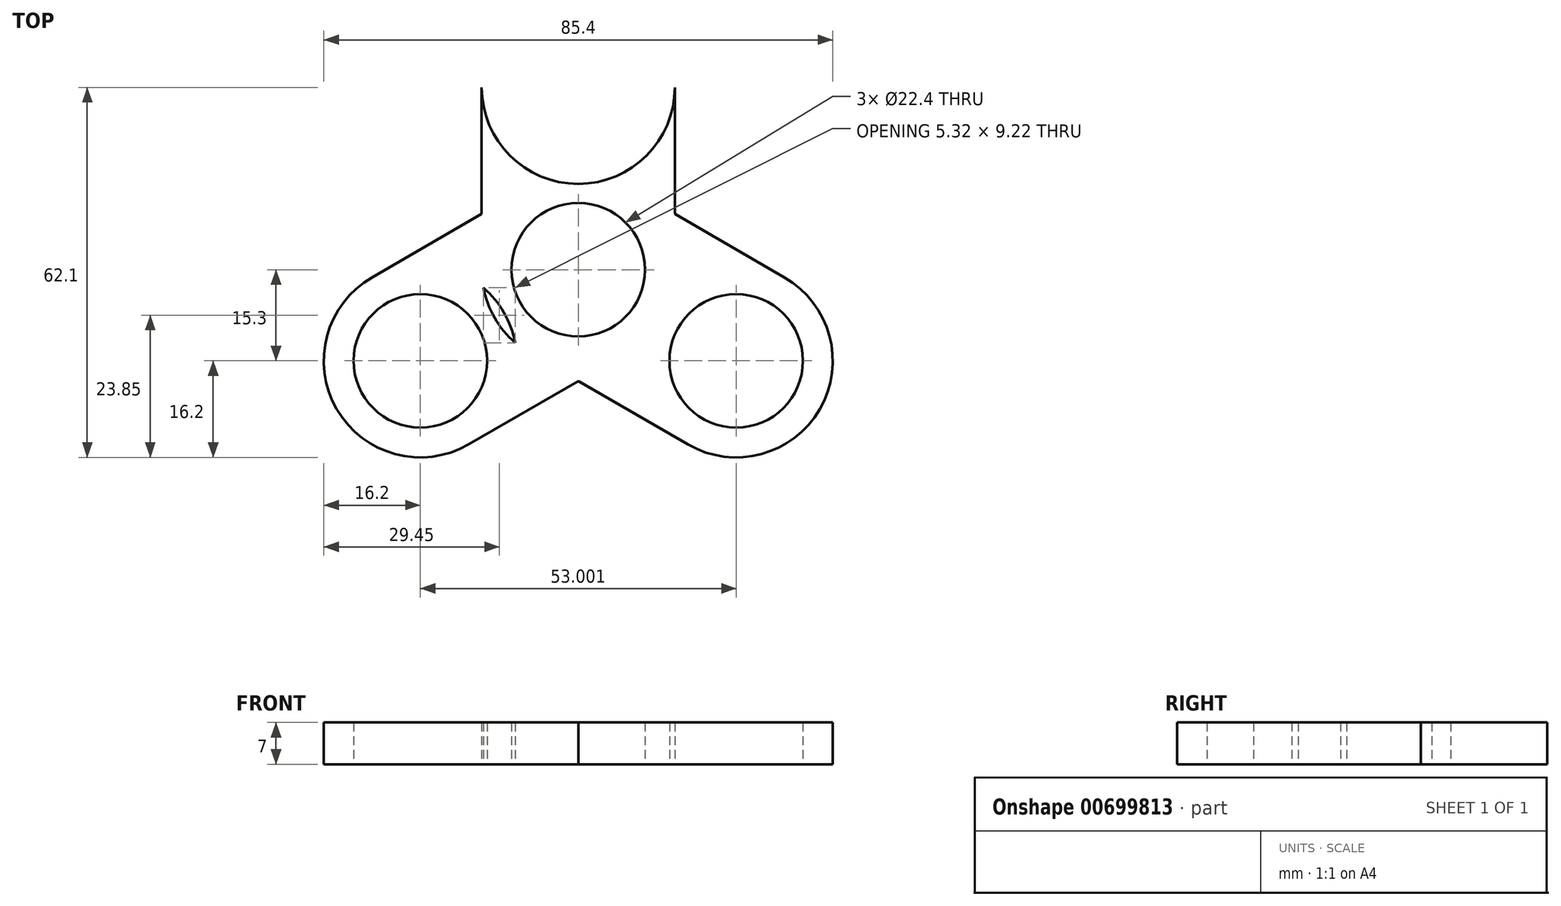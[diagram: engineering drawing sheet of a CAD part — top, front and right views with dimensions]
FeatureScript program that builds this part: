
annotation { "Feature Type Name" : "Feature", "Feature Type Description" : "" }
export const myFeature = defineFeature(function(context is Context, id is Id, definition is map)
    precondition{}
    {
        {
            var Q0;
            Q0=qCreatedBy(makeId("Top.planeOp"),FACE);
            var sketch = newSketch(context, id + "F0", { "sketchPlane" : qUnion([Q0])});
            skCircle(sketch, "E0", {"center": v(0, 0) * mm, "radius": 11.2 * mm});
            skCircle(sketch, "E1", {"center": v(0, 0) * mm, "radius": 50 * mm});
            skLineSegment(sketch, "E2", {"start": v(0, 50) * mm, "end": v(0, 11.2) * mm});
            skCircle(sketch, "E3", {"center": v(0, 30.6) * mm, "radius": 11.2 * mm});
            skCircle(sketch, "E4", {"center": v(0, 0) * mm, "radius": 16.2 * mm});
            skCircle(sketch, "E5", {"center": v(0, 30.6) * mm, "radius": 16.2 * mm});
            skLineSegment(sketch, "E6", {"start": v(16.2, 30.6) * mm, "end": v(16.2, 0) * mm});
            skLineSegment(sketch, "E7", {"start": v(0, 60) * mm, "end": v(0, -58.02) * mm, "construction": true});
            skLineSegment(sketch, "E8.MirrorCS", {"start": v(-16.2, 30.6) * mm, "end": v(-16.2, 0) * mm});
            skLineSegment(sketch, "E9.1.0", {"start": v(-18.4, -29.33) * mm, "end": v(8.1, -14.03) * mm});
            skCircle(sketch, "E9.1.2", {"center": v(-26.5, -15.3) * mm, "radius": 16.2 * mm});
            skCircle(sketch, "E9.1.3", {"center": v(-26.5, -15.3) * mm, "radius": 11.2 * mm});
            skLineSegment(sketch, "E9.1.4", {"start": v(-34.6, -1.27) * mm, "end": v(-8.1, 14.03) * mm});
            skLineSegment(sketch, "E9.2.0", {"start": v(34.6, -1.27) * mm, "end": v(8.1, 14.03) * mm});
            skCircle(sketch, "E9.2.2", {"center": v(26.5, -15.3) * mm, "radius": 16.2 * mm});
            skCircle(sketch, "E9.2.3", {"center": v(26.5, -15.3) * mm, "radius": 11.2 * mm});
            skLineSegment(sketch, "E9.2.4", {"start": v(18.4, -29.33) * mm, "end": v(-8.1, -14.03) * mm});
            skSolve(sketch);
        }
        {
            var Q0;
            Q0=makeQuery(id+"F0.imprint","IMPRINT",FACE,{"disambiguationData":[TD([[makeQuery(id+"F0.imprint","IMPRINT",EDGE,{"derivedFrom":sQuery(id+"F0.wireOp",EDGE,"E9.1.3")}),-1.0]])]});
            var Q1;
            {var subQ0=sQuery(id+"F0.wireOp",EDGE,"E4");var subQ1=sQuery(id+"F0.wireOp",EDGE,"E8.MirrorCS");var subQ2=makeQuery(id+"F0.imprint","INTERSECT",VERTEX,{"derivedFrom":[subQ1,subQ0]});Q1=makeQuery(id+"F0.imprint","IMPRINT",FACE,{"disambiguationData":[TD([[makeQuery(id+"F0.imprint","IMPRINT",EDGE,{"disambiguationData":[TD([[subQ2,1.0]])],"derivedFrom":subQ1}),-1.0]])]});}
            var Q2;
            {var subQ0=sQuery(id+"F0.wireOp",EDGE,"E4");var subQ1=sQuery(id+"F0.wireOp",EDGE,"E9.1.2");var subQ2=makeQuery(id+"F0.imprint","INTERSECT",VERTEX,{"disambiguationData":[OD(0.0)],"derivedFrom":[subQ1,subQ0]});Q2=makeQuery(id+"F0.imprint","IMPRINT",FACE,{"disambiguationData":[TD([[makeQuery(id+"F0.imprint","IMPRINT",EDGE,{"disambiguationData":[TD([[subQ2,-1.0]])],"derivedFrom":subQ1}),1.0]])]});}
            var Q3;
            Q3=makeQuery(id+"F0.imprint","IMPRINT",FACE,{"disambiguationData":[TD([[makeQuery(id+"F0.imprint","IMPRINT",EDGE,{"derivedFrom":sQuery(id+"F0.wireOp",EDGE,"E0")}),-1.0]])]});
            var Q4;
            {var subQ0=sQuery(id+"F0.wireOp",EDGE,"E4");var subQ1=sQuery(id+"F0.wireOp",EDGE,"E8.MirrorCS");var subQ2=makeQuery(id+"F0.imprint","INTERSECT",VERTEX,{"derivedFrom":[subQ1,subQ0]});Q4=makeQuery(id+"F0.imprint","IMPRINT",FACE,{"disambiguationData":[TD([[makeQuery(id+"F0.imprint","IMPRINT",EDGE,{"disambiguationData":[TD([[subQ2,1.0]])],"derivedFrom":subQ1}),1.0]])]});}
            var Q5;
            {var subQ0=sQuery(id+"F0.wireOp",EDGE,"E8.MirrorCS");var subQ1=sQuery(id+"F0.wireOp",EDGE,"E5");var subQ2=makeQuery(id+"F0.imprint","INTERSECT",VERTEX,{"derivedFrom":[subQ1,subQ0]});Q5=makeQuery(id+"F0.imprint","IMPRINT",FACE,{"disambiguationData":[TD([[makeQuery(id+"F0.imprint","IMPRINT",EDGE,{"disambiguationData":[TD([[subQ2,-1.0]])],"derivedFrom":subQ1}),-1.0]])]});}
            var Q6;
            {var subQ0=sQuery(id+"F0.wireOp",EDGE,"E5");var subQ1=sQuery(id+"F0.wireOp",EDGE,"E2");var subQ2=makeQuery(id+"F0.imprint","INTERSECT",VERTEX,{"disambiguationData":[OD(1.0)],"derivedFrom":[subQ1,subQ0]});Q6=makeQuery(id+"F0.imprint","IMPRINT",FACE,{"disambiguationData":[TD([[makeQuery(id+"F0.imprint","IMPRINT",EDGE,{"disambiguationData":[TD([[subQ2,1.0]])],"derivedFrom":subQ1}),1.0]])]});}
            var Q7;
            {var subQ0=sQuery(id+"F0.wireOp",EDGE,"E5");var subQ1=sQuery(id+"F0.wireOp",EDGE,"E2");var subQ2=makeQuery(id+"F0.imprint","INTERSECT",VERTEX,{"disambiguationData":[OD(1.0)],"derivedFrom":[subQ1,subQ0]});Q7=makeQuery(id+"F0.imprint","IMPRINT",FACE,{"disambiguationData":[TD([[makeQuery(id+"F0.imprint","IMPRINT",EDGE,{"disambiguationData":[TD([[subQ2,1.0]])],"derivedFrom":subQ1}),-1.0]])]});}
            var Q8;
            {var subQ1=sQuery(id+"F0.wireOp",EDGE,"E2");var subQ4=sQuery(id+"F0.wireOp",EDGE,"E5");var subQ6=makeQuery(id+"F0.imprint","INTERSECT",VERTEX,{"disambiguationData":[OD(0.0)],"derivedFrom":[subQ1,subQ4]});Q8=makeQuery(id+"F0.imprint","IMPRINT",FACE,{"disambiguationData":[TD([[makeQuery(id+"F0.imprint","IMPRINT",EDGE,{"disambiguationData":[TD([[subQ6,-1.0]])],"derivedFrom":subQ1}),-1.0]])]});}
            var Q9;
            {var subQ0=sQuery(id+"F0.wireOp",EDGE,"E5");var subQ2=sQuery(id+"F0.wireOp",EDGE,"E2");var subQ3=makeQuery(id+"F0.imprint","INTERSECT",VERTEX,{"disambiguationData":[OD(0.0)],"derivedFrom":[subQ2,subQ0]});Q9=makeQuery(id+"F0.imprint","IMPRINT",FACE,{"disambiguationData":[TD([[makeQuery(id+"F0.imprint","IMPRINT",EDGE,{"disambiguationData":[TD([[subQ3,-1.0]])],"derivedFrom":subQ2}),1.0]])]});}
            var Q10;
            {var subQ0=sQuery(id+"F0.wireOp",EDGE,"E4");var subQ1=sQuery(id+"F0.wireOp",EDGE,"E6");var subQ2=makeQuery(id+"F0.imprint","INTERSECT",VERTEX,{"derivedFrom":[subQ1,subQ0]});Q10=makeQuery(id+"F0.imprint","IMPRINT",FACE,{"disambiguationData":[TD([[makeQuery(id+"F0.imprint","IMPRINT",EDGE,{"disambiguationData":[TD([[subQ2,1.0]])],"derivedFrom":subQ1}),-1.0]])]});}
            var Q11;
            {var subQ0=sQuery(id+"F0.wireOp",EDGE,"E6");var subQ1=sQuery(id+"F0.wireOp",EDGE,"E5");var subQ2=makeQuery(id+"F0.imprint","INTERSECT",VERTEX,{"derivedFrom":[subQ1,subQ0]});Q11=makeQuery(id+"F0.imprint","IMPRINT",FACE,{"disambiguationData":[TD([[makeQuery(id+"F0.imprint","IMPRINT",EDGE,{"disambiguationData":[TD([[subQ2,1.0]])],"derivedFrom":subQ1}),-1.0]])]});}
            var Q12;
            {var subQ0=sQuery(id+"F0.wireOp",EDGE,"E4");var subQ1=sQuery(id+"F0.wireOp",EDGE,"E6");var subQ2=makeQuery(id+"F0.imprint","INTERSECT",VERTEX,{"derivedFrom":[subQ1,subQ0]});Q12=makeQuery(id+"F0.imprint","IMPRINT",FACE,{"disambiguationData":[TD([[makeQuery(id+"F0.imprint","IMPRINT",EDGE,{"disambiguationData":[TD([[subQ2,1.0]])],"derivedFrom":subQ1}),1.0]])]});}
            var Q13;
            {var subQ0=sQuery(id+"F0.wireOp",EDGE,"E4");var subQ1=sQuery(id+"F0.wireOp",EDGE,"E9.1.0");var subQ2=makeQuery(id+"F0.imprint","INTERSECT",VERTEX,{"derivedFrom":[subQ1,subQ0]});Q13=makeQuery(id+"F0.imprint","IMPRINT",FACE,{"disambiguationData":[TD([[makeQuery(id+"F0.imprint","IMPRINT",EDGE,{"disambiguationData":[TD([[subQ2,1.0]])],"derivedFrom":subQ1}),-1.0]])]});}
            var Q14;
            {var subQ0=sQuery(id+"F0.wireOp",EDGE,"E9.1.2");var subQ1=sQuery(id+"F0.wireOp",EDGE,"E9.1.0");var subQ2=makeQuery(id+"F0.imprint","INTERSECT",VERTEX,{"derivedFrom":[subQ1,subQ0]});Q14=makeQuery(id+"F0.imprint","IMPRINT",FACE,{"disambiguationData":[TD([[makeQuery(id+"F0.imprint","IMPRINT",EDGE,{"disambiguationData":[TD([[subQ2,-1.0]])],"derivedFrom":subQ1}),1.0]])]});}
            var Q15;
            Q15=makeQuery(id+"F0.imprint","IMPRINT",FACE,{"disambiguationData":[TD([[makeQuery(id+"F0.imprint","IMPRINT",EDGE,{"derivedFrom":sQuery(id+"F0.wireOp",EDGE,"E9.2.3")}),-1.0]])]});
            var Q16;
            {var subQ0=sQuery(id+"F0.wireOp",EDGE,"E4");var subQ1=sQuery(id+"F0.wireOp",EDGE,"E9.1.0");var subQ2=makeQuery(id+"F0.imprint","INTERSECT",VERTEX,{"derivedFrom":[subQ1,subQ0]});Q16=makeQuery(id+"F0.imprint","IMPRINT",FACE,{"disambiguationData":[TD([[makeQuery(id+"F0.imprint","IMPRINT",EDGE,{"disambiguationData":[TD([[subQ2,1.0]])],"derivedFrom":subQ1}),1.0]])]});}
            var Q17;
            {var subQ0=sQuery(id+"F0.wireOp",EDGE,"E9.2.2");var subQ1=sQuery(id+"F0.wireOp",EDGE,"E4");var subQ2=makeQuery(id+"F0.imprint","INTERSECT",VERTEX,{"disambiguationData":[OD(0.0)],"derivedFrom":[subQ1,subQ0]});Q17=makeQuery(id+"F0.imprint","IMPRINT",FACE,{"disambiguationData":[TD([[makeQuery(id+"F0.imprint","IMPRINT",EDGE,{"disambiguationData":[TD([[subQ2,-1.0]])],"derivedFrom":subQ1}),1.0]])]});}
            extrude(context, id + "F1", {"entities" : qUnion([Q0, Q1, Q2, Q3, Q4, Q5, Q6, Q7, Q8, Q9, Q10, Q11, Q12, Q13, Q14, Q15, Q16, Q17]), "depth" : 7 * mm, "offsetDistance" : 25.4 * mm});
        }
    });
